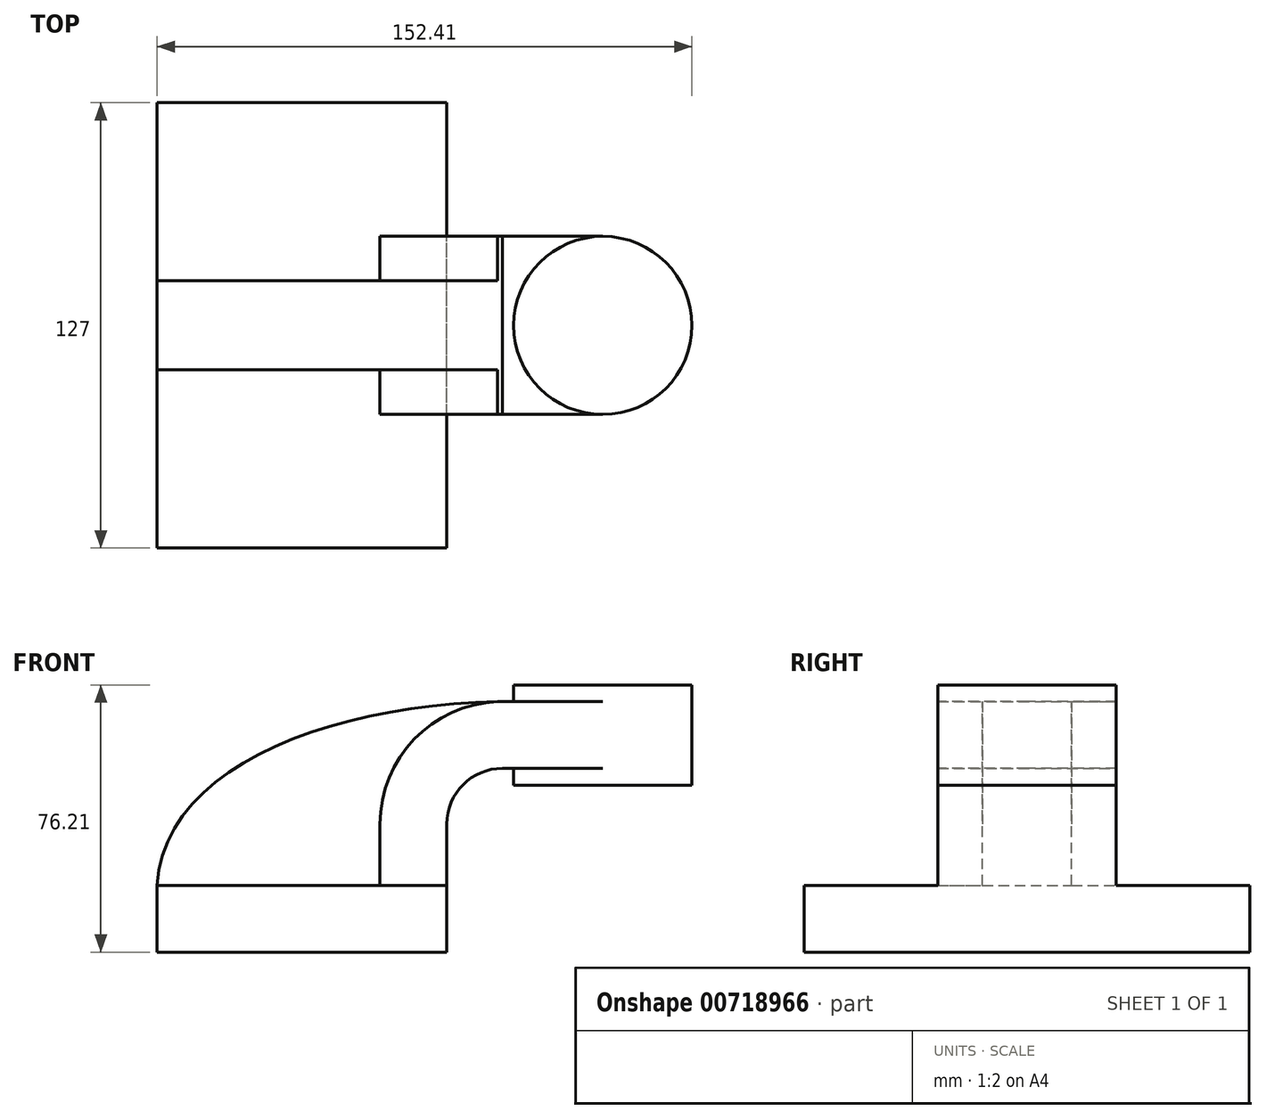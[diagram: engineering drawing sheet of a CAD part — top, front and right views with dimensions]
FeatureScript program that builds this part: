
annotation { "Feature Type Name" : "Feature", "Feature Type Description" : "" }
export const myFeature = defineFeature(function(context is Context, id is Id, definition is map)
    precondition{}
    {
        {
            var Q0;
            Q0=qCreatedBy(makeId("Front.planeOp"),FACE);
            var sketch = newSketch(context, id + "F0", { "sketchPlane" : qUnion([Q0])});
            skLineSegment(sketch, "E0.bottom", {"start": v(41.28, -9.52) * mm, "end": v(-41.28, -9.53) * mm});
            skLineSegment(sketch, "E0.top", {"start": v(41.28, 9.53) * mm, "end": v(-41.28, 9.53) * mm});
            skLineSegment(sketch, "E0.left", {"start": v(41.28, -9.52) * mm, "end": v(41.28, 9.53) * mm});
            skLineSegment(sketch, "E0.right", {"start": v(-41.28, -9.53) * mm, "end": v(-41.28, 9.53) * mm});
            skPoint(sketch, "E0.middle", {"position": v(0, 0) * mm});
            skLineSegment(sketch, "E1.bottom", {"start": v(111.12, 38.1) * mm, "end": v(60.33, 38.1) * mm});
            skLineSegment(sketch, "E1.top", {"start": v(111.12, 66.68) * mm, "end": v(60.33, 66.68) * mm});
            skLineSegment(sketch, "E1.left", {"start": v(111.12, 38.1) * mm, "end": v(111.12, 66.68) * mm});
            skLineSegment(sketch, "E1.right", {"start": v(60.32, 38.1) * mm, "end": v(60.33, 66.68) * mm});
            skPoint(sketch, "E1.middle", {"position": v(85.72, 52.39) * mm});
            skLineSegment(sketch, "E2", {"start": v(41.28, 9.53) * mm, "end": v(41.28, 27) * mm});
            skArc(sketch, "E3", {"start": v(41.27, 27) * mm, "mid": v(45.92, 38.23) * mm, "end": v(57.15, 42.88) * mm});
            skLineSegment(sketch, "E4", {"start": v(57.15, 42.88) * mm, "end": v(107.95, 42.88) * mm});
            skLineSegment(sketch, "E5.0", {"start": v(57.15, 61.93) * mm, "end": v(107.95, 61.93) * mm});
            skArc(sketch, "E5.1", {"start": v(22.23, 27) * mm, "mid": v(32.45, 51.7) * mm, "end": v(57.15, 61.93) * mm});
            skLineSegment(sketch, "E5.2", {"start": v(22.23, 9.53) * mm, "end": v(22.23, 27) * mm});
            skLineSegment(sketch, "E6", {"start": v(85.72, 38.1) * mm, "end": v(85.72, 66.68) * mm});
            skFitSpline(sketch, "E7", {"points": [v(-41.28, 9.53) * mm, v(57.15, 61.93) * mm], "startDerivative": vector(6.26, 102.77) * mm, "endDerivative": vector(145.5, 2.4) * mm});
            skSolve(sketch);
        }
        {
            var Q0;
            Q0=makeQuery(id+"F0.imprint","IMPRINT",FACE,{"disambiguationData":[TD([[makeQuery(id+"F0.imprint","IMPRINT",EDGE,{"derivedFrom":sQuery(id+"F0.wireOp",EDGE,"E0.bottom")}),-1.0]])]});
            extrude(context, id + "F1", {"entities" : qUnion([Q0]), "endBound" : BoundingType.SYMMETRIC, "depth" : 127 * mm, "offsetDistance" : 25.4 * mm});
        }
        {
            var Q0;
            {var subQ1=sQuery(id+"F0.wireOp",EDGE,"E2");Q0=makeQuery(id+"F0.imprint","IMPRINT",FACE,{"disambiguationData":[TD([[makeQuery(id+"F0.imprint","IMPRINT",EDGE,{"derivedFrom":subQ1}),1.0]])]});}
            var Q1;
            {var subQ0=sQuery(id+"F0.wireOp",EDGE,"E4");var subQ1=sQuery(id+"F0.wireOp",EDGE,"E1.right");var subQ2=makeQuery(id+"F0.imprint","INTERSECT",VERTEX,{"derivedFrom":[subQ1,subQ0]});Q1=makeQuery(id+"F0.imprint","IMPRINT",FACE,{"disambiguationData":[TD([[makeQuery(id+"F0.imprint","IMPRINT",EDGE,{"disambiguationData":[TD([[subQ2,-1.0]])],"derivedFrom":subQ1}),-1.0]])]});}
            extrude(context, id + "F2", {"entities" : qUnion([Q0, Q1]), "operationType" : NewBodyOperationType.ADD, "endBound" : BoundingType.SYMMETRIC, "depth" : 50.8 * mm, "offsetDistance" : 25.4 * mm});
        }
        {
            var Q0;
            {var subQ3=sQuery(id+"F0.wireOp",EDGE,"E5.2");Q0=makeQuery(id+"F0.imprint","IMPRINT",FACE,{"disambiguationData":[TD([[makeQuery(id+"F0.imprint","IMPRINT",EDGE,{"derivedFrom":subQ3}),1.0]])]});}
            extrude(context, id + "F3", {"entities" : qUnion([Q0]), "operationType" : NewBodyOperationType.ADD, "endBound" : BoundingType.SYMMETRIC, "depth" : 25.4 * mm, "offsetDistance" : 25.4 * mm});
        }
        {
            var Q0;
            {var subQ0=sQuery(id+"F0.wireOp",EDGE,"E1.left");Q0=makeQuery(id+"F0.imprint","IMPRINT",FACE,{"disambiguationData":[TD([[makeQuery(id+"F0.imprint","IMPRINT",EDGE,{"derivedFrom":subQ0}),1.0]])]});}
            var Q1;
            Q1=sQuery(id+"F0.wireOp",EDGE,"E6");
            revolve(context, id + "F4", {"operationType" : NewBodyOperationType.ADD, "surfaceOperationType" : NewSurfaceOperationType.NEW, "entities" : qUnion([Q0]), "axis" : qUnion([Q1]), "revolveType" : RevolveType.FULL});
        }
    });
